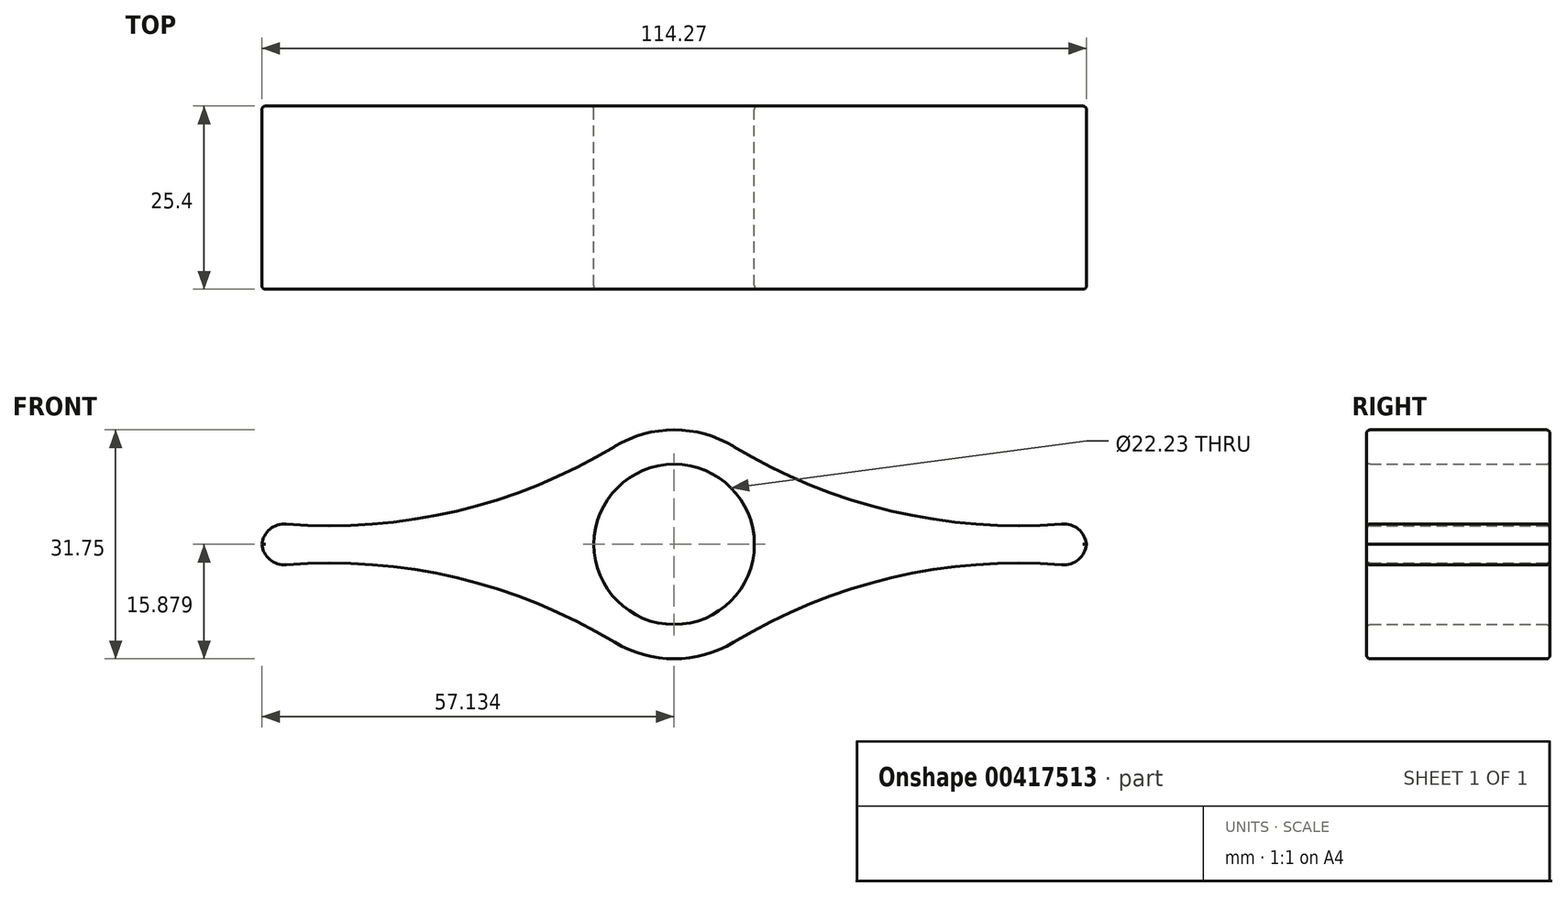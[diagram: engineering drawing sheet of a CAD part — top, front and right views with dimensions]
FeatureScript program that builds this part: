
annotation { "Feature Type Name" : "Feature", "Feature Type Description" : "" }
export const myFeature = defineFeature(function(context is Context, id is Id, definition is map)
    precondition{}
    {
        {
            var Q0;
            Q0=qCreatedBy(makeId("Front.planeOp"),FACE);
            var sketch = newSketch(context, id + "F0", { "sketchPlane" : qUnion([Q0])});
            skCircle(sketch, "E0", {"center": v(-41.59, 27.2) * mm, "radius": 11.11 * mm});
            skCircle(sketch, "E1", {"center": v(-41.59, 27.2) * mm, "radius": 15.88 * mm});
            skLineSegment(sketch, "E2", {"start": v(-41.59, 27.2) * mm, "end": v(15.56, 27.2) * mm, "construction": true});
            skLineSegment(sketch, "E3", {"start": v(15.56, 27.2) * mm, "end": v(15.56, 30.37) * mm});
            skArc(sketch, "E4", {"start": v(-33.37, 40.78) * mm, "mid": v(-9.78, 31.45) * mm, "end": v(15.56, 30.37) * mm});
            skArc(sketch, "E5.MirrorCS", {"start": v(-33.37, 13.62) * mm, "mid": v(-9.78, 22.95) * mm, "end": v(15.56, 24.02) * mm});
            skLineSegment(sketch, "E6", {"start": v(-41.59, 27.2) * mm, "end": v(-41.59, 43.07) * mm, "construction": true});
            skArc(sketch, "E7.MirrorCS", {"start": v(-49.8, 40.78) * mm, "mid": v(-73.4, 31.45) * mm, "end": v(-98.74, 30.37) * mm});
            skArc(sketch, "E8.MirrorCS", {"start": v(-49.8, 13.62) * mm, "mid": v(-73.4, 22.95) * mm, "end": v(-98.74, 24.02) * mm});
            skLineSegment(sketch, "E9.MirrorCS", {"start": v(-98.74, 27.2) * mm, "end": v(-98.74, 30.37) * mm});
            skLineSegment(sketch, "E10.MirrorCS", {"start": v(15.56, 27.2) * mm, "end": v(15.56, 24.02) * mm});
            skLineSegment(sketch, "E11.MirrorCS", {"start": v(-98.74, 27.2) * mm, "end": v(-98.74, 24.02) * mm});
            skSolve(sketch);
        }
        {
            var Q0;
            Q0=qSketchRegion(id+"F0",true);
            extrude(context, id + "F1", {"entities" : qUnion([Q0]), "depth" : 25.4 * mm});
        }
        {
            var Q0;
            Q0=makeQuery(id+"F1.opExtrude","SWEPT_EDGE",EDGE,{"disambiguationData":[OSD([sQuery(id+"F0.wireOp",EDGE,"E3"),sQuery(id+"F0.wireOp",EDGE,"E4")])]});
            var Q1;
            Q1=makeQuery(id+"F1.opExtrude","SWEPT_EDGE",EDGE,{"disambiguationData":[OSD([sQuery(id+"F0.wireOp",EDGE,"E5.MirrorCS"),sQuery(id+"F0.wireOp",EDGE,"E10.MirrorCS")])]});
            var Q2;
            Q2=makeQuery(id+"F1.opExtrude","SWEPT_EDGE",EDGE,{"disambiguationData":[OSD([sQuery(id+"F0.wireOp",EDGE,"E7.MirrorCS"),sQuery(id+"F0.wireOp",EDGE,"E9.MirrorCS")])]});
            var Q3;
            Q3=makeQuery(id+"F1.opExtrude","SWEPT_EDGE",EDGE,{"disambiguationData":[OSD([sQuery(id+"F0.wireOp",EDGE,"E8.MirrorCS"),sQuery(id+"F0.wireOp",EDGE,"E11.MirrorCS")])]});
            fillet(context, id + "F2", {"entities" : qUnion([Q0, Q1, Q2, Q3]), "radius" : 3.17 * mm, "tangentPropagation" : true, "allowEdgeOverflow" : false});
        }
        {
            var Q0;
            Q0=makeQuery(id+"F1.opExtrude","CAP_EDGE",EDGE,{"disambiguationData":[OSD([sQuery(id+"F0.wireOp",EDGE,"E7.MirrorCS")])],"isStart":false});
            var Q1;
            Q1=makeQuery(id+"F1.opExtrude","CAP_EDGE",EDGE,{"disambiguationData":[OSD([sQuery(id+"F0.wireOp",EDGE,"E4")])],"isStart":true});
            var Q2;
            Q2=makeQuery(id+"F1.opExtrude","CAP_EDGE",EDGE,{"disambiguationData":[OSD([sQuery(id+"F0.wireOp",EDGE,"E5.MirrorCS")])],"isStart":false});
            var Q3;
            Q3=makeQuery(id+"F1.opExtrude","CAP_EDGE",EDGE,{"disambiguationData":[OSD([sQuery(id+"F0.wireOp",EDGE,"E5.MirrorCS")])],"isStart":true});
            var Q4;
            Q4=makeQuery(id+"F1.opExtrude","CAP_EDGE",EDGE,{"disambiguationData":[OSD([sQuery(id+"F0.wireOp",EDGE,"E0")])],"isStart":false});
            var Q5;
            Q5=makeQuery(id+"F1.opExtrude","CAP_EDGE",EDGE,{"disambiguationData":[OSD([sQuery(id+"F0.wireOp",EDGE,"E0")])],"isStart":true});
            fillet(context, id + "F3", {"entities" : qUnion([Q0, Q1, Q2, Q3, Q4, Q5]), "radius" : 0.5 * mm, "tangentPropagation" : true, "allowEdgeOverflow" : false});
        }
    });
